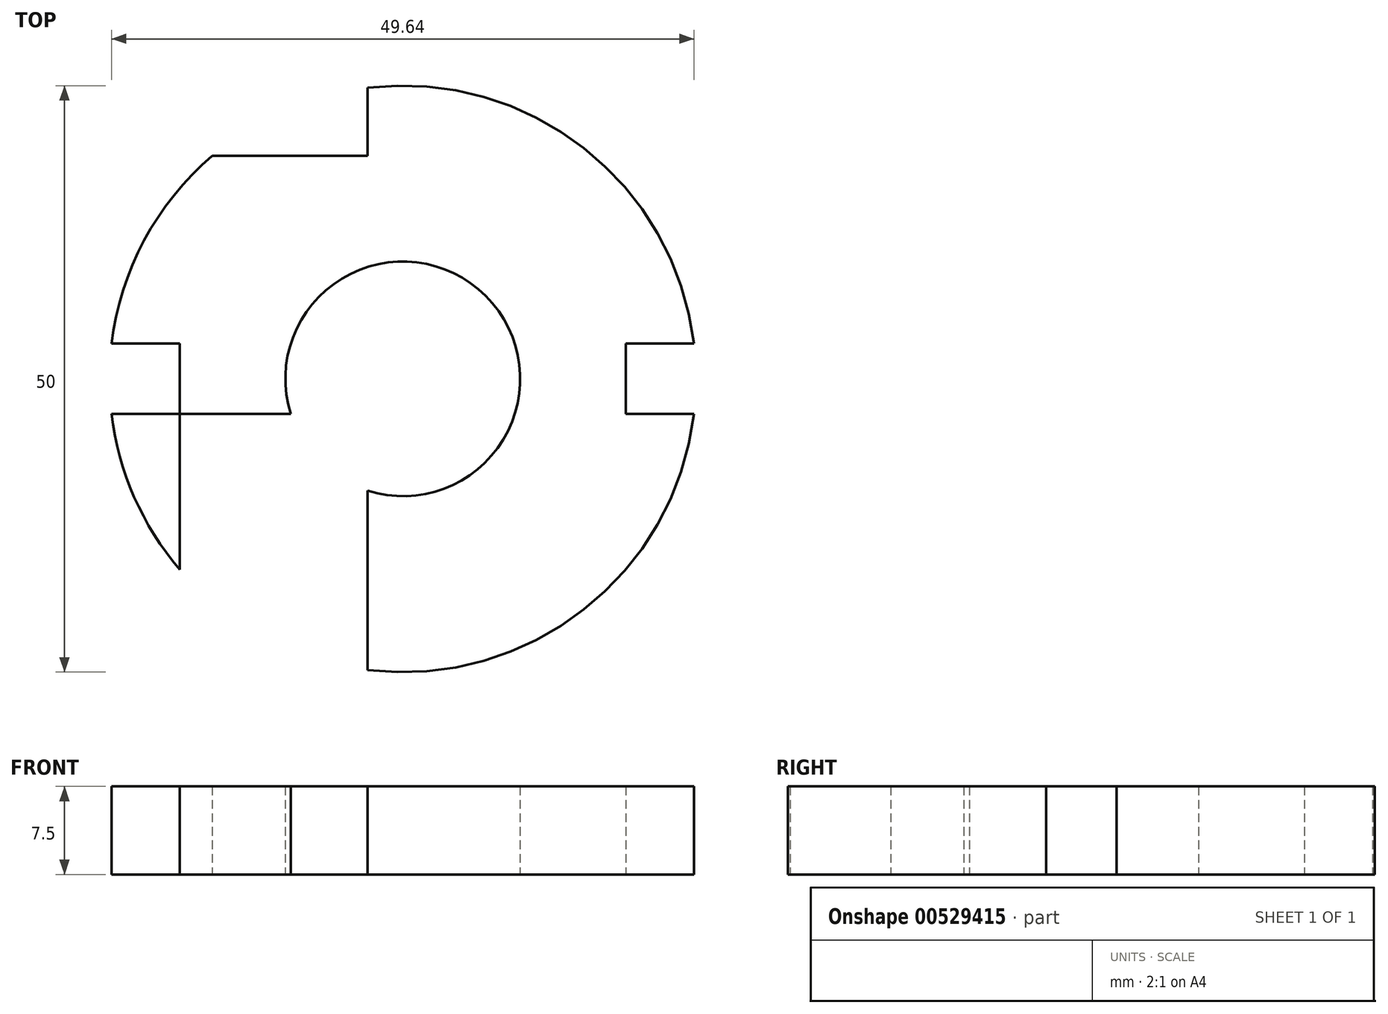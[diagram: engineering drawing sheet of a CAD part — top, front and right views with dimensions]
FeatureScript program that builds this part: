
annotation { "Feature Type Name" : "Feature", "Feature Type Description" : "" }
export const myFeature = defineFeature(function(context is Context, id is Id, definition is map)
    precondition{}
    {
        {
            var Q0;
            Q0=qCreatedBy(makeId("Top.planeOp"),FACE);
            var sketch = newSketch(context, id + "F0", { "sketchPlane" : qUnion([Q0])});
            skCircle(sketch, "E0", {"center": v(0, 0) * mm, "radius": 10 * mm});
            skCircle(sketch, "E1", {"center": v(0, 0) * mm, "radius": 25 * mm});
            skLineSegment(sketch, "E2", {"start": v(-25, 0) * mm, "end": v(25, 0) * mm, "construction": true});
            skLineSegment(sketch, "E3", {"start": v(0, -25) * mm, "end": v(0, 25) * mm, "construction": true});
            skLineSegment(sketch, "E4.0", {"start": v(3, -25) * mm, "end": v(3, 25) * mm});
            skLineSegment(sketch, "E5.0", {"start": v(-3, -25) * mm, "end": v(-3, 25) * mm});
            skLineSegment(sketch, "E6.0", {"start": v(-25, -3) * mm, "end": v(-19, -3) * mm});
            skLineSegment(sketch, "E7.0", {"start": v(-25, 3) * mm, "end": v(-19, 3) * mm});
            skLineSegment(sketch, "E8.0", {"start": v(19, -25) * mm, "end": v(19, -3) * mm});
            skLineSegment(sketch, "E9.0", {"start": v(-25, -19) * mm, "end": v(-3, -19) * mm});
            skLineSegment(sketch, "E10.MirrorCS", {"start": v(-25, 19) * mm, "end": v(-3, 19) * mm});
            skLineSegment(sketch, "E11.MirrorCS", {"start": v(-19, -25) * mm, "end": v(-19, 25) * mm});
            skLineSegment(sketch, "E12", {"start": v(-3, 19) * mm, "end": v(3, 19) * mm});
            skLineSegment(sketch, "E13", {"start": v(3, 19) * mm, "end": v(25, 19) * mm});
            skLineSegment(sketch, "E14", {"start": v(19, 3) * mm, "end": v(19, 25) * mm});
            skLineSegment(sketch, "E15", {"start": v(19, -3) * mm, "end": v(19, 3) * mm});
            skLineSegment(sketch, "E16", {"start": v(3, -19) * mm, "end": v(25, -19) * mm});
            skLineSegment(sketch, "E17", {"start": v(-3, -19) * mm, "end": v(3, -19) * mm});
            skLineSegment(sketch, "E18", {"start": v(-19, -3) * mm, "end": v(25, -3) * mm});
            skLineSegment(sketch, "E19", {"start": v(-19, 3) * mm, "end": v(25, 3) * mm});
            skSolve(sketch);
        }
        {
            var Q0;
            {var subQ1=sQuery(id+"F0.wireOp",EDGE,"E4.0");var subQ5=sQuery(id+"F0.wireOp",EDGE,"E0");var subQ6=makeQuery(id+"F0.imprint","INTERSECT",VERTEX,{"disambiguationData":[OD(0.0)],"derivedFrom":[subQ5,subQ1]});Q0=makeQuery(id+"F0.imprint","IMPRINT",FACE,{"disambiguationData":[TD([[makeQuery(id+"F0.imprint","IMPRINT",EDGE,{"disambiguationData":[TD([[subQ6,1.0]])],"derivedFrom":subQ5}),-1.0]])]});}
            var Q1;
            {var subQ0=sQuery(id+"F0.wireOp",EDGE,"E4.0");var subQ1=sQuery(id+"F0.wireOp",EDGE,"E1");var subQ2=makeQuery(id+"F0.imprint","INTERSECT",VERTEX,{"disambiguationData":[OD(0.0)],"derivedFrom":[subQ1,subQ0]});Q1=makeQuery(id+"F0.imprint","IMPRINT",FACE,{"disambiguationData":[TD([[makeQuery(id+"F0.imprint","IMPRINT",EDGE,{"disambiguationData":[TD([[subQ2,1.0]])],"derivedFrom":subQ1}),1.0]])]});}
            var Q2;
            {var subQ0=sQuery(id+"F0.wireOp",EDGE,"E5.0");var subQ1=sQuery(id+"F0.wireOp",EDGE,"E1");var subQ2=makeQuery(id+"F0.imprint","INTERSECT",VERTEX,{"disambiguationData":[OD(0.0)],"derivedFrom":[subQ1,subQ0]});Q2=makeQuery(id+"F0.imprint","IMPRINT",FACE,{"disambiguationData":[TD([[makeQuery(id+"F0.imprint","IMPRINT",EDGE,{"disambiguationData":[TD([[subQ2,-1.0]])],"derivedFrom":subQ1}),1.0]])]});}
            var Q3;
            {var subQ1=sQuery(id+"F0.wireOp",EDGE,"E5.0");var subQ5=sQuery(id+"F0.wireOp",EDGE,"E0");var subQ6=makeQuery(id+"F0.imprint","INTERSECT",VERTEX,{"disambiguationData":[OD(0.0)],"derivedFrom":[subQ5,subQ1]});Q3=makeQuery(id+"F0.imprint","IMPRINT",FACE,{"disambiguationData":[TD([[makeQuery(id+"F0.imprint","IMPRINT",EDGE,{"disambiguationData":[TD([[subQ6,-1.0]])],"derivedFrom":subQ5}),-1.0]])]});}
            var Q4;
            {var subQ0=sQuery(id+"F0.wireOp",EDGE,"E7.0");var subQ1=sQuery(id+"F0.wireOp",EDGE,"E1");var subQ2=makeQuery(id+"F0.imprint","INTERSECT",VERTEX,{"derivedFrom":[subQ1,subQ0]});Q4=makeQuery(id+"F0.imprint","IMPRINT",FACE,{"disambiguationData":[TD([[makeQuery(id+"F0.imprint","IMPRINT",EDGE,{"disambiguationData":[TD([[subQ2,1.0]])],"derivedFrom":subQ1}),1.0]])]});}
            var Q5;
            {var subQ0=sQuery(id+"F0.wireOp",EDGE,"E19");var subQ1=sQuery(id+"F0.wireOp",EDGE,"E0");var subQ2=makeQuery(id+"F0.imprint","INTERSECT",VERTEX,{"disambiguationData":[OD(1.0)],"derivedFrom":[subQ1,subQ0]});Q5=makeQuery(id+"F0.imprint","IMPRINT",FACE,{"disambiguationData":[TD([[makeQuery(id+"F0.imprint","IMPRINT",EDGE,{"disambiguationData":[TD([[subQ2,-1.0]])],"derivedFrom":subQ1}),-1.0]])]});}
            var Q6;
            {var subQ5=sQuery(id+"F0.wireOp",EDGE,"E0");var subQ9=sQuery(id+"F0.wireOp",EDGE,"E18");var subQ10=makeQuery(id+"F0.imprint","INTERSECT",VERTEX,{"disambiguationData":[OD(0.0)],"derivedFrom":[subQ5,subQ9]});Q6=makeQuery(id+"F0.imprint","IMPRINT",FACE,{"disambiguationData":[TD([[makeQuery(id+"F0.imprint","IMPRINT",EDGE,{"disambiguationData":[TD([[subQ10,-1.0]])],"derivedFrom":subQ5}),-1.0]])]});}
            var Q7;
            {var subQ0=sQuery(id+"F0.wireOp",EDGE,"E6.0");var subQ1=sQuery(id+"F0.wireOp",EDGE,"E1");var subQ2=makeQuery(id+"F0.imprint","INTERSECT",VERTEX,{"derivedFrom":[subQ1,subQ0]});Q7=makeQuery(id+"F0.imprint","IMPRINT",FACE,{"disambiguationData":[TD([[makeQuery(id+"F0.imprint","IMPRINT",EDGE,{"disambiguationData":[TD([[subQ2,-1.0]])],"derivedFrom":subQ1}),1.0]])]});}
            var Q8;
            {var subQ0=sQuery(id+"F0.wireOp",EDGE,"E5.0");var subQ1=sQuery(id+"F0.wireOp",EDGE,"E1");var subQ2=makeQuery(id+"F0.imprint","INTERSECT",VERTEX,{"disambiguationData":[OD(1.0)],"derivedFrom":[subQ1,subQ0]});Q8=makeQuery(id+"F0.imprint","IMPRINT",FACE,{"disambiguationData":[TD([[makeQuery(id+"F0.imprint","IMPRINT",EDGE,{"disambiguationData":[TD([[subQ2,1.0]])],"derivedFrom":subQ1}),1.0]])]});}
            var Q9;
            {var subQ0=sQuery(id+"F0.wireOp",EDGE,"E4.0");var subQ1=sQuery(id+"F0.wireOp",EDGE,"E1");var subQ2=makeQuery(id+"F0.imprint","INTERSECT",VERTEX,{"disambiguationData":[OD(1.0)],"derivedFrom":[subQ1,subQ0]});Q9=makeQuery(id+"F0.imprint","IMPRINT",FACE,{"disambiguationData":[TD([[makeQuery(id+"F0.imprint","IMPRINT",EDGE,{"disambiguationData":[TD([[subQ2,-1.0]])],"derivedFrom":subQ1}),1.0]])]});}
            var Q10;
            {var subQ1=sQuery(id+"F0.wireOp",EDGE,"E4.0");var subQ3=sQuery(id+"F0.wireOp",EDGE,"E0");var subQ4=makeQuery(id+"F0.imprint","INTERSECT",VERTEX,{"disambiguationData":[OD(1.0)],"derivedFrom":[subQ3,subQ1]});Q10=makeQuery(id+"F0.imprint","IMPRINT",FACE,{"disambiguationData":[TD([[makeQuery(id+"F0.imprint","IMPRINT",EDGE,{"disambiguationData":[TD([[subQ4,-1.0]])],"derivedFrom":subQ3}),-1.0]])]});}
            var Q11;
            {var subQ0=sQuery(id+"F0.wireOp",EDGE,"E18");var subQ1=sQuery(id+"F0.wireOp",EDGE,"E1");var subQ2=makeQuery(id+"F0.imprint","INTERSECT",VERTEX,{"derivedFrom":[subQ1,subQ0]});Q11=makeQuery(id+"F0.imprint","IMPRINT",FACE,{"disambiguationData":[TD([[makeQuery(id+"F0.imprint","IMPRINT",EDGE,{"disambiguationData":[TD([[subQ2,1.0]])],"derivedFrom":subQ1}),1.0]])]});}
            var Q12;
            {var subQ0=sQuery(id+"F0.wireOp",EDGE,"E19");var subQ1=sQuery(id+"F0.wireOp",EDGE,"E1");var subQ2=makeQuery(id+"F0.imprint","INTERSECT",VERTEX,{"derivedFrom":[subQ1,subQ0]});Q12=makeQuery(id+"F0.imprint","IMPRINT",FACE,{"disambiguationData":[TD([[makeQuery(id+"F0.imprint","IMPRINT",EDGE,{"disambiguationData":[TD([[subQ2,-1.0]])],"derivedFrom":subQ1}),1.0]])]});}
            var Q13;
            {var subQ5=sQuery(id+"F0.wireOp",EDGE,"E15");Q13=makeQuery(id+"F0.imprint","IMPRINT",FACE,{"disambiguationData":[TD([[makeQuery(id+"F0.imprint","IMPRINT",EDGE,{"derivedFrom":subQ5}),1.0]])]});}
            var Q14;
            {var subQ5=sQuery(id+"F0.wireOp",EDGE,"E17");Q14=makeQuery(id+"F0.imprint","IMPRINT",FACE,{"disambiguationData":[TD([[makeQuery(id+"F0.imprint","IMPRINT",EDGE,{"derivedFrom":subQ5}),1.0]])]});}
            var Q15;
            {var subQ5=sQuery(id+"F0.wireOp",EDGE,"E12");Q15=makeQuery(id+"F0.imprint","IMPRINT",FACE,{"disambiguationData":[TD([[makeQuery(id+"F0.imprint","IMPRINT",EDGE,{"derivedFrom":subQ5}),-1.0]])]});}
            extrude(context, id + "F1", {"entities" : qUnion([Q0, Q1, Q2, Q3, Q4, Q5, Q6, Q7, Q8, Q9, Q10, Q11, Q12, Q13, Q14, Q15]), "depth" : 7.5 * mm, "offsetDistance" : 25 * mm});
        }
    });
